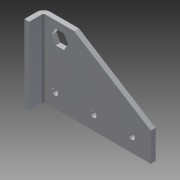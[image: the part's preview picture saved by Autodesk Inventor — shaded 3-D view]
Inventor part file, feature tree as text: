
AUTODESK INVENTOR PART (.ipt)
format: ipt  version: 2014 (Build 180170000, 170)  size: 118,784 bytes
history: native  units: in
note: dims shown in document units (in); Inventor stores cm internally (conversion verified against a paired STEP export)
features: sheet_metal_op x4, sketch x2, other x2
ambient origin geometry x8: Origin, YZ Plane, XZ Plane, XY Plane, X Axis, Y Axis, Z Axis, Center Point
bodies: Solid1 (feature_tree)
feature tree (8):
  sheet_metal_op  "Face1"
  sheet_metal_op  "Flange2"
  sketch  "Sketch1"  dims[d5=2.75in d6=0.163in d7=0.25in d8=0.375in]
  other  "Plate1"
  sketch  "Sketch3"  dims[d11=0.125in d22=1.1811in d24=1.0in d25=0.3937in d27=1.0in d29=2.0in d30=0.75in d31=0.75in d32=0.375in d34=0.375in d35=0.375in d36=0.125in d37=0.0625in d38=0.25in d39=0.125in d40=0.5in d41=90.0deg d42=0.05in d43=0.5in d44=0.125in d45=0.125in]
  other  "Plate3"
  sheet_metal_op  "Bend2"
  sheet_metal_op  "Corner2"
